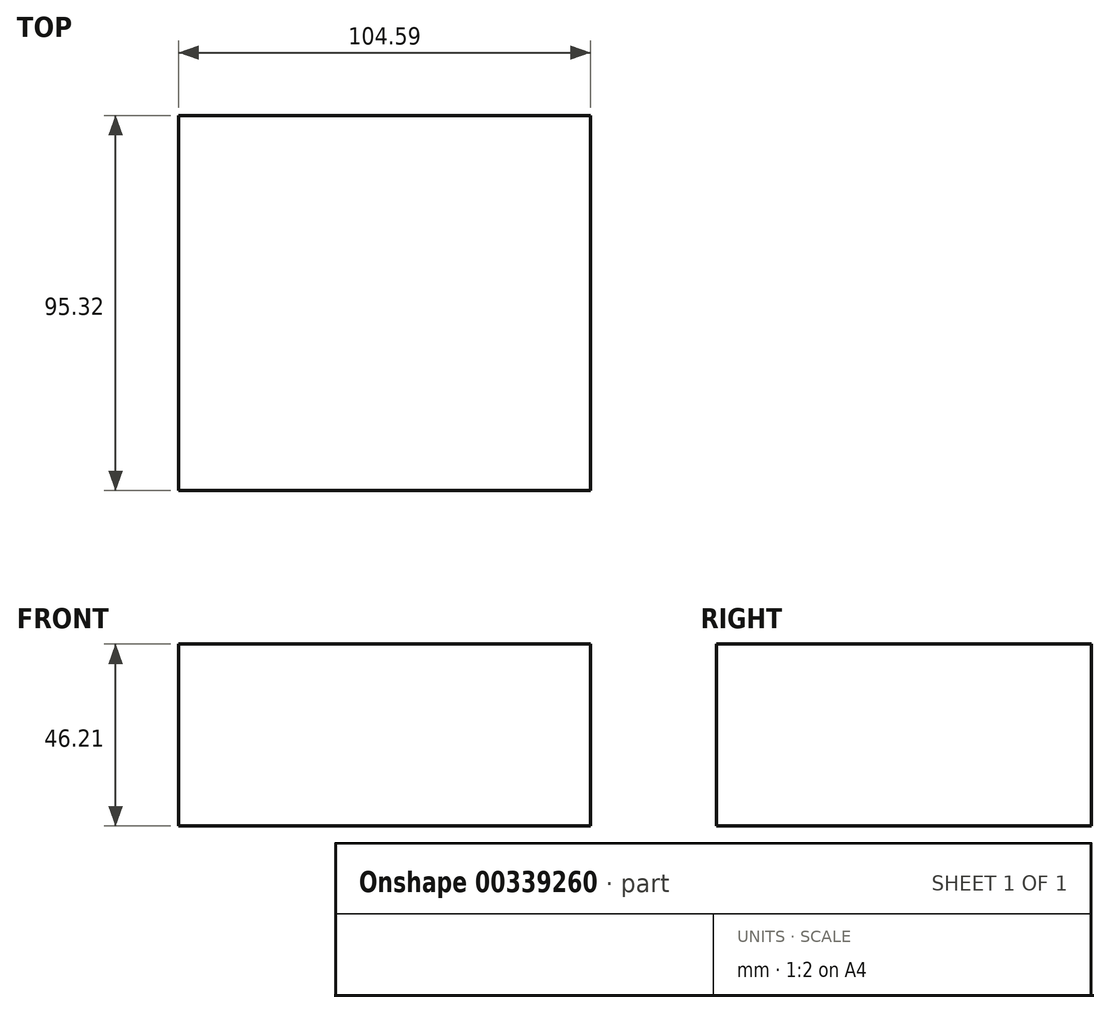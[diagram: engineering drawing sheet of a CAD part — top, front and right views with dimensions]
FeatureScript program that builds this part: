
annotation { "Feature Type Name" : "Feature", "Feature Type Description" : "" }
export const myFeature = defineFeature(function(context is Context, id is Id, definition is map)
    precondition{}
    {
        {
            var Q0;
            Q0=qCreatedBy(makeId("Top.planeOp"),FACE);
            var sketch = newSketch(context, id + "F0", { "sketchPlane" : qUnion([Q0])});
            skLineSegment(sketch, "E0.bottom", {"start": v(-67.2, -56.92) * mm, "end": v(37.38, -56.92) * mm});
            skLineSegment(sketch, "E0.top", {"start": v(-67.2, 38.4) * mm, "end": v(37.38, 38.4) * mm});
            skLineSegment(sketch, "E0.left", {"start": v(-67.2, -56.92) * mm, "end": v(-67.2, 38.4) * mm});
            skLineSegment(sketch, "E0.right", {"start": v(37.38, -56.92) * mm, "end": v(37.38, 38.4) * mm});
            skSolve(sketch);
        }
        {
            var Q0;
            Q0=makeQuery(id+"F0.imprint","IMPRINT",FACE,{"disambiguationData":[TD([[makeQuery(id+"F0.imprint","IMPRINT",EDGE,{"derivedFrom":sQuery(id+"F0.wireOp",EDGE,"E0.bottom")}),1.0]])]});
            extrude(context, id + "F1", {"entities" : qUnion([Q0]), "depth" : 46.2 * mm});
        }
    });
